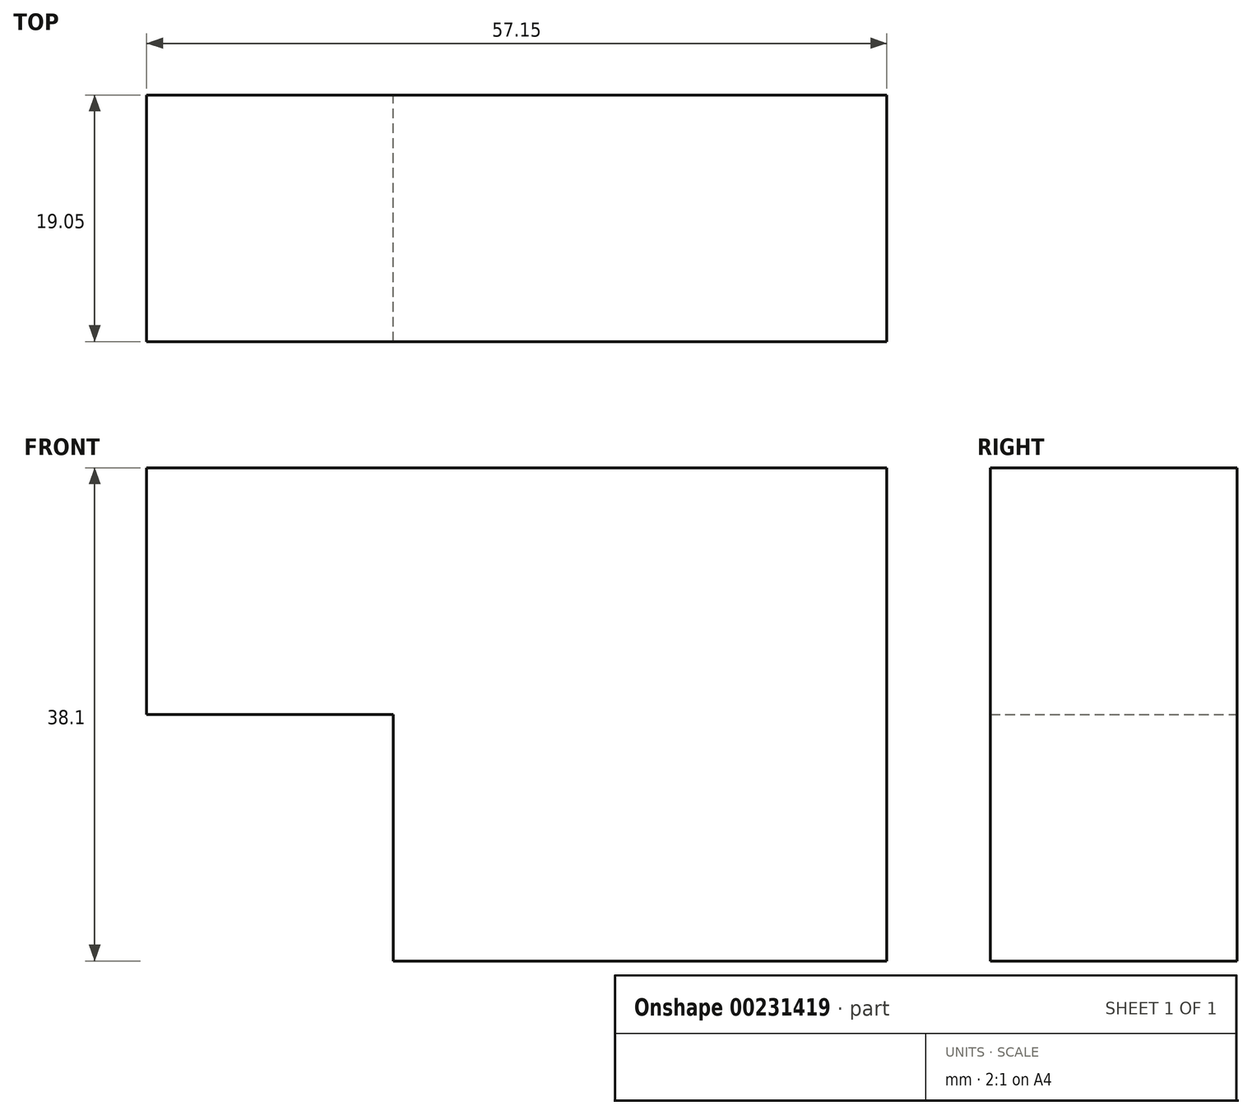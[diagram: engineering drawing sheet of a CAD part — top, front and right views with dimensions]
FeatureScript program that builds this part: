
annotation { "Feature Type Name" : "Feature", "Feature Type Description" : "" }
export const myFeature = defineFeature(function(context is Context, id is Id, definition is map)
    precondition{}
    {
        {
            var Q0;
            Q0=qCreatedBy(makeId("Front.planeOp"),FACE);
            var sketch = newSketch(context, id + "F0", { "sketchPlane" : qUnion([Q0])});
            skLineSegment(sketch, "E0.bottom", {"start": v(-38.08, 27.81) * mm, "end": v(19.07, 27.81) * mm});
            skLineSegment(sketch, "E0.top", {"start": v(-38.08, 8.76) * mm, "end": v(19.07, 8.76) * mm});
            skLineSegment(sketch, "E0.left", {"start": v(-38.08, 27.81) * mm, "end": v(-38.08, 8.76) * mm});
            skLineSegment(sketch, "E0.right", {"start": v(19.07, 27.81) * mm, "end": v(19.07, 8.76) * mm});
            skLineSegment(sketch, "E1.bottom", {"start": v(19.07, 8.76) * mm, "end": v(-19.03, 8.76) * mm});
            skLineSegment(sketch, "E1.top", {"start": v(19.07, -10.29) * mm, "end": v(-19.03, -10.29) * mm});
            skLineSegment(sketch, "E1.left", {"start": v(19.07, 8.76) * mm, "end": v(19.07, -10.29) * mm});
            skLineSegment(sketch, "E1.right", {"start": v(-19.03, 8.76) * mm, "end": v(-19.03, -10.29) * mm});
            skSolve(sketch);
        }
        {
            var Q0;
            Q0 = qSketchRegion(id + "F0", true);
            extrude(context, id + "F1", {"entities" : qUnion([Q0]), "depth" : 19.05 * mm});
        }
    });
